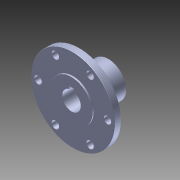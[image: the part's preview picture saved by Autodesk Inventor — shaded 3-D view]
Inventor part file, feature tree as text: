
AUTODESK INVENTOR PART (.ipt)
format: ipt  version: 2014 (Build 180170000, 170)  size: 151,040 bytes
history: native  units: in
note: dims shown in document units (in); Inventor stores cm internally (conversion verified against a paired STEP export)
features: chamfer x1, other x1, imported_body x1
ambient origin geometry x8: Origin, YZ Plane, XZ Plane, XY Plane, X Axis, Y Axis, Z Axis, Center Point
bodies: Body1 (feature_tree)
feature tree (3):
  chamfer  "Chamfer2"  [1 undecoded]
  other  "am-0077a-500 Key Hub r21"
  imported_body  "Base1"
note: 1 required parameter value undecoded (feature->parameter linkage not recoverable at this tier; creation-order binding heuristic only, values carry confidence <= 0.55)
